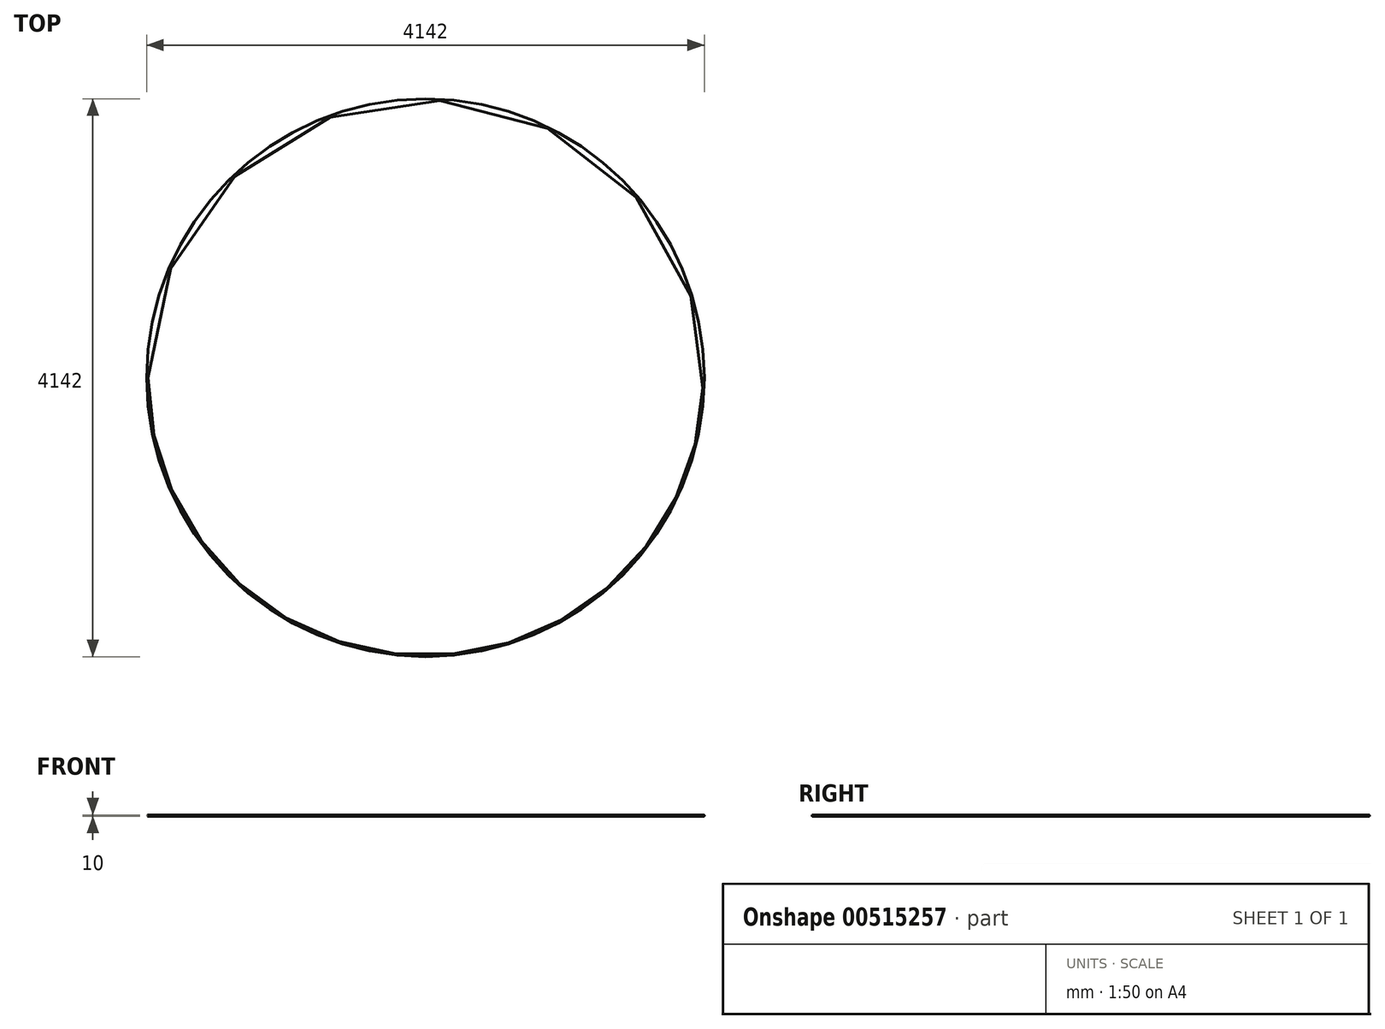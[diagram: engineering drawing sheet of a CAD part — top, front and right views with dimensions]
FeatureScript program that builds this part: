
annotation { "Feature Type Name" : "Feature", "Feature Type Description" : "" }
export const myFeature = defineFeature(function(context is Context, id is Id, definition is map)
    precondition{}
    {
        {
            var Q0;
            Q0=qCreatedBy(makeId("Right.planeOp"),FACE);
            var sketch = newSketch(context, id + "F0", { "sketchPlane" : qUnion([Q0])});
            skCircle(sketch, "E0", {"center": v(2066, 0) * mm, "radius": 5 * mm});
            skLineSegment(sketch, "E1", {"start": v(0, 0) * mm, "end": v(0, 513.48) * mm, "construction": true});
            skSolve(sketch);
        }
        {
            var Q0;
            Q0 = qSketchRegion(id + "F0", true);
            var Q1;
            Q1=sQuery(id+"F0.wireOp",EDGE,"E1");
            revolve(context, id + "F1", {"entities" : qUnion([Q0]), "axis" : qUnion([Q1]), "revolveType" : RevolveType.FULL});
        }
    });
